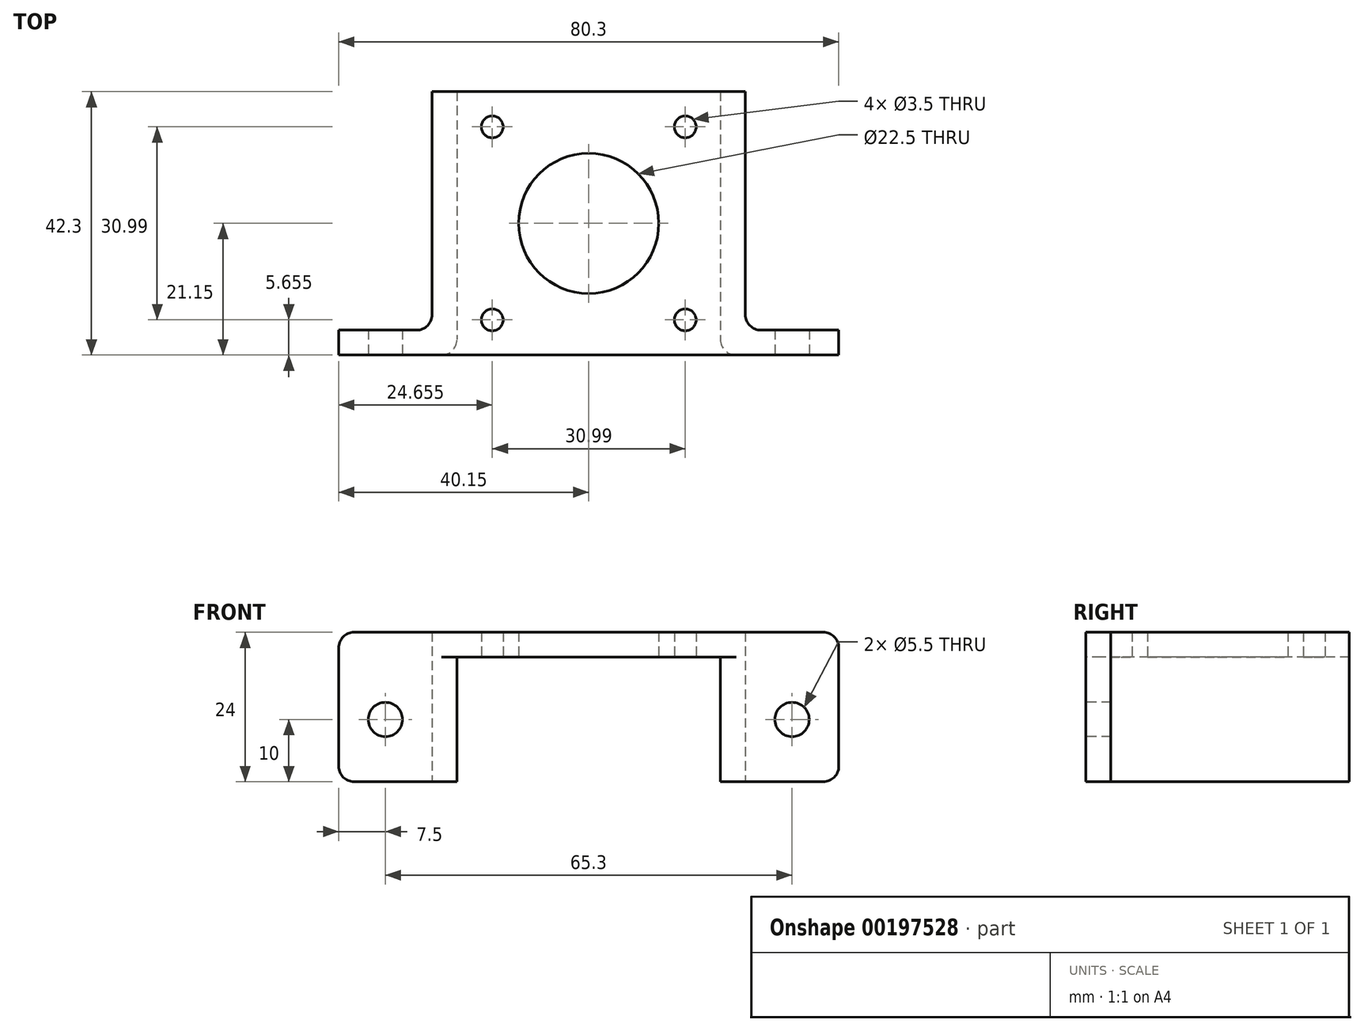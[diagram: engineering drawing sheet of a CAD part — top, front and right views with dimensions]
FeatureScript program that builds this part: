
annotation { "Feature Type Name" : "Feature", "Feature Type Description" : "" }
export const myFeature = defineFeature(function(context is Context, id is Id, definition is map)
    precondition{}
    {
        {
            var Q0;
            Q0=qCreatedBy(makeId("Top.planeOp"),FACE);
            var sketch = newSketch(context, id + "F0", { "sketchPlane" : qUnion([Q0])});
            skLineSegment(sketch, "E0.bottom", {"start": v(-21.15, 21.15) * mm, "end": v(21.15, 21.15) * mm});
            skLineSegment(sketch, "E0.left", {"start": v(-21.15, 21.15) * mm, "end": v(-21.15, -21.15) * mm, "construction": true});
            skLineSegment(sketch, "E0.right", {"start": v(21.15, 21.15) * mm, "end": v(21.15, -21.15) * mm, "construction": true});
            skLineSegment(sketch, "E1.bottom", {"start": v(-15.5, 15.5) * mm, "end": v(15.5, 15.5) * mm, "construction": true});
            skLineSegment(sketch, "E1.top", {"start": v(-15.5, -15.5) * mm, "end": v(15.5, -15.5) * mm, "construction": true});
            skLineSegment(sketch, "E1.left", {"start": v(-15.5, 15.5) * mm, "end": v(-15.5, -15.5) * mm, "construction": true});
            skLineSegment(sketch, "E1.right", {"start": v(15.5, 15.5) * mm, "end": v(15.5, -15.5) * mm, "construction": true});
            skCircle(sketch, "E2", {"center": v(-15.5, 15.5) * mm, "radius": 1.75 * mm});
            skCircle(sketch, "E3", {"center": v(-15.5, -15.5) * mm, "radius": 1.75 * mm});
            skCircle(sketch, "E4", {"center": v(15.5, 15.5) * mm, "radius": 1.75 * mm});
            skCircle(sketch, "E5", {"center": v(15.5, -15.5) * mm, "radius": 1.75 * mm});
            skCircle(sketch, "E6", {"center": v(0, 0) * mm, "radius": 11.25 * mm});
            skLineSegment(sketch, "E7", {"start": v(-21.15, -21.15) * mm, "end": v(21.15, -21.15) * mm});
            skLineSegment(sketch, "E8.bottom", {"start": v(21.15, -21.15) * mm, "end": v(40.15, -21.15) * mm});
            skLineSegment(sketch, "E8.top", {"start": v(21.15, -17.15) * mm, "end": v(40.15, -17.15) * mm});
            skLineSegment(sketch, "E8.left", {"start": v(21.15, -21.15) * mm, "end": v(21.15, -17.15) * mm});
            skLineSegment(sketch, "E8.right", {"start": v(40.15, -21.15) * mm, "end": v(40.15, -17.15) * mm});
            skLineSegment(sketch, "E9.bottom", {"start": v(-21.15, -21.15) * mm, "end": v(-40.15, -21.15) * mm});
            skLineSegment(sketch, "E9.top", {"start": v(-21.15, -17.15) * mm, "end": v(-40.15, -17.15) * mm});
            skLineSegment(sketch, "E9.left", {"start": v(-21.15, -21.15) * mm, "end": v(-21.15, -17.15) * mm});
            skLineSegment(sketch, "E9.right", {"start": v(-40.15, -21.15) * mm, "end": v(-40.15, -17.15) * mm});
            skLineSegment(sketch, "E10.bottom", {"start": v(-21.15, 21.15) * mm, "end": v(-25.15, 21.15) * mm});
            skLineSegment(sketch, "E10.top", {"start": v(-21.15, -17.15) * mm, "end": v(-25.15, -17.15) * mm});
            skLineSegment(sketch, "E10.left", {"start": v(-21.15, 21.15) * mm, "end": v(-21.15, -17.15) * mm});
            skLineSegment(sketch, "E10.right", {"start": v(-25.15, 21.15) * mm, "end": v(-25.15, -17.15) * mm});
            skLineSegment(sketch, "E11.bottom", {"start": v(21.15, 21.15) * mm, "end": v(25.15, 21.15) * mm});
            skLineSegment(sketch, "E11.top", {"start": v(21.15, -17.15) * mm, "end": v(25.15, -17.15) * mm});
            skLineSegment(sketch, "E11.left", {"start": v(21.15, 21.15) * mm, "end": v(21.15, -17.15) * mm});
            skLineSegment(sketch, "E11.right", {"start": v(25.15, 21.15) * mm, "end": v(25.15, -17.15) * mm});
            skSolve(sketch);
        }
        {
            var Q0;
            Q0=qSketchRegion(id+"F0",true);
            extrude(context, id + "F1", {"entities" : qUnion([Q0]), "depth" : 4 * mm});
        }
        {
            var Q0;
            Q0=makeQuery(id+"F1.opExtrude","CAP_FACE",FACE,{"disambiguationData":[OSD([sQuery(id+"F0.wireOp",EDGE,"E0.bottom"),sQuery(id+"F0.wireOp",EDGE,"E2"),sQuery(id+"F0.wireOp",EDGE,"E3"),sQuery(id+"F0.wireOp",EDGE,"E4"),sQuery(id+"F0.wireOp",EDGE,"E5"),sQuery(id+"F0.wireOp",EDGE,"E6"),sQuery(id+"F0.wireOp",EDGE,"E7"),sQuery(id+"F0.wireOp",EDGE,"E8.bottom"),sQuery(id+"F0.wireOp",EDGE,"E8.top"),sQuery(id+"F0.wireOp",EDGE,"E8.right"),sQuery(id+"F0.wireOp",EDGE,"E9.bottom"),sQuery(id+"F0.wireOp",EDGE,"E9.top"),sQuery(id+"F0.wireOp",EDGE,"E9.right"),sQuery(id+"F0.wireOp",EDGE,"E10.bottom"),sQuery(id+"F0.wireOp",EDGE,"E10.right"),sQuery(id+"F0.wireOp",EDGE,"E11.bottom"),sQuery(id+"F0.wireOp",EDGE,"E11.right")])],"isStart":true});
            var sketch = newSketch(context, id + "F2", { "sketchPlane" : qUnion([Q0])});
            skLineSegment(sketch, "E12.0", {"start": v(-21.15, -21.15) * mm, "end": v(-21.15, 17.15) * mm});
            skLineSegment(sketch, "E13.0", {"start": v(-21.15, 21.15) * mm, "end": v(-21.15, 17.15) * mm});
            skLineSegment(sketch, "E14.0", {"start": v(-21.15, 21.15) * mm, "end": v(-40.15, 21.15) * mm});
            skLineSegment(sketch, "E15.0", {"start": v(-40.15, 21.15) * mm, "end": v(-40.15, 17.15) * mm});
            skLineSegment(sketch, "E16.0", {"start": v(-25.15, -21.15) * mm, "end": v(-25.15, 17.15) * mm});
            skLineSegment(sketch, "E17.0", {"start": v(-25.15, 17.15) * mm, "end": v(-40.15, 17.15) * mm});
            skLineSegment(sketch, "E18.0", {"start": v(-21.15, -21.15) * mm, "end": v(-25.15, -21.15) * mm});
            skLineSegment(sketch, "E19.0", {"start": v(21.15, -21.15) * mm, "end": v(25.15, -21.15) * mm});
            skLineSegment(sketch, "E20.0", {"start": v(21.15, -21.15) * mm, "end": v(21.15, 17.15) * mm});
            skLineSegment(sketch, "E21.0", {"start": v(25.15, -21.15) * mm, "end": v(25.15, 17.15) * mm});
            skLineSegment(sketch, "E22.0", {"start": v(25.15, 17.15) * mm, "end": v(40.15, 17.15) * mm});
            skLineSegment(sketch, "E23.0", {"start": v(40.15, 21.15) * mm, "end": v(40.15, 17.15) * mm});
            skLineSegment(sketch, "E24.0", {"start": v(21.15, 21.15) * mm, "end": v(40.15, 21.15) * mm});
            skLineSegment(sketch, "E25.0", {"start": v(21.15, 21.15) * mm, "end": v(21.15, 17.15) * mm});
            skPoint(sketch, "E26.orphan", {"position": v(-21.15, 17.15) * mm});
            skPoint(sketch, "E27.orphan", {"position": v(21.15, 17.15) * mm});
            skSolve(sketch);
        }
        {
            var Q0;
            Q0=qSketchRegion(id+"F2",true);
            extrude(context, id + "F3", {"entities" : qUnion([Q0]), "operationType" : NewBodyOperationType.ADD, "depth" : 20 * mm});
        }
        {
            var Q0;
            Q0=makeQuery(id+"F3.boolean.opBoolean","MERGE",FACE,{"derivedFrom":[makeQuery(id+"F1.opExtrude","SWEPT_FACE",FACE,{"disambiguationData":[OSD([sQuery(id+"F0.wireOp",EDGE,"E7"),sQuery(id+"F0.wireOp",EDGE,"E8.bottom"),sQuery(id+"F0.wireOp",EDGE,"E9.bottom")])]}),makeQuery(id+"F3.opExtrude","SWEPT_FACE",FACE,{"disambiguationData":[OSD([sQuery(id+"F2.wireOp",EDGE,"E14.0")])]}),makeQuery(id+"F3.opExtrude","SWEPT_FACE",FACE,{"disambiguationData":[OSD([sQuery(id+"F2.wireOp",EDGE,"E24.0")])]})]});
            var sketch = newSketch(context, id + "F4", { "sketchPlane" : qUnion([Q0])});
            skCircle(sketch, "E28", {"center": v(-32.65, -10) * mm, "radius": 2.75 * mm});
            skPoint(sketch, "E28.centerSnap1", {"position": v(-21.15, -10) * mm});
            skCircle(sketch, "E29", {"center": v(32.65, -10) * mm, "radius": 2.75 * mm});
            skPoint(sketch, "E29.centerSnap0", {"position": v(21.15, -10) * mm});
            skSolve(sketch);
        }
        {
            var Q0;
            Q0=qSketchRegion(id+"F4",true);
            extrude(context, id + "F5", {"entities" : qUnion([Q0]), "operationType" : NewBodyOperationType.REMOVE, "endBound" : BoundingType.UP_TO_NEXT, "oppositeDirection" : true, "depth" : 25 * mm});
        }
        {
            var Q0;
            Q0=makeQuery(id+"F1.opExtrude","CAP_EDGE",EDGE,{"disambiguationData":[OSD([sQuery(id+"F0.wireOp",EDGE,"E9.right")])],"isStart":false});
            var Q1;
            Q1=makeQuery(id+"F3.opExtrude","CAP_EDGE",EDGE,{"disambiguationData":[OSD([sQuery(id+"F2.wireOp",EDGE,"E15.0")])],"isStart":false});
            var Q2;
            Q2=makeQuery(id+"F3.opExtrude","CAP_EDGE",EDGE,{"disambiguationData":[OSD([sQuery(id+"F2.wireOp",EDGE,"E23.0")])],"isStart":false});
            var Q3;
            Q3=makeQuery(id+"F1.opExtrude","CAP_EDGE",EDGE,{"disambiguationData":[OSD([sQuery(id+"F0.wireOp",EDGE,"E8.right")])],"isStart":false});
            var Q4;
            Q4=makeQuery(id+"F3.boolean.opBoolean","MERGE",EDGE,{"derivedFrom":[makeQuery(id+"F1.opExtrude","SWEPT_EDGE",EDGE,{"disambiguationData":[OSD([sQuery(id+"F0.wireOp",EDGE,"E8.top"),sQuery(id+"F0.wireOp",EDGE,"E11.top"),sQuery(id+"F0.wireOp",EDGE,"E11.right")])]}),makeQuery(id+"F3.opExtrude","SWEPT_EDGE",EDGE,{"disambiguationData":[OSD([sQuery(id+"F2.wireOp",EDGE,"E21.0"),sQuery(id+"F2.wireOp",EDGE,"E22.0")])]})]});
            var Q5;
            Q5=makeQuery(id+"F3.boolean.opBoolean","MERGE",EDGE,{"derivedFrom":[makeQuery(id+"F1.opExtrude","SWEPT_EDGE",EDGE,{"disambiguationData":[OSD([sQuery(id+"F0.wireOp",EDGE,"E9.top"),sQuery(id+"F0.wireOp",EDGE,"E10.top"),sQuery(id+"F0.wireOp",EDGE,"E10.right")])]}),makeQuery(id+"F3.opExtrude","SWEPT_EDGE",EDGE,{"disambiguationData":[OSD([sQuery(id+"F2.wireOp",EDGE,"E16.0"),sQuery(id+"F2.wireOp",EDGE,"E17.0")])]})]});
            var Q6;
            Q6=makeQuery(id+"F3.opExtrude","SWEPT_EDGE",EDGE,{"disambiguationData":[OSD([sQuery(id+"F0.wireOp",EDGE,"E7"),sQuery(id+"F0.wireOp",EDGE,"E8.bottom"),sQuery(id+"F0.wireOp",EDGE,"E9.bottom"),sQuery(id+"F2.wireOp",EDGE,"E24.0"),sQuery(id+"F2.wireOp",EDGE,"E25.0")])]});
            var Q7;
            Q7=makeQuery(id+"F3.opExtrude","SWEPT_EDGE",EDGE,{"disambiguationData":[OSD([sQuery(id+"F0.wireOp",EDGE,"E7"),sQuery(id+"F0.wireOp",EDGE,"E8.bottom"),sQuery(id+"F0.wireOp",EDGE,"E9.bottom"),sQuery(id+"F2.wireOp",EDGE,"E13.0"),sQuery(id+"F2.wireOp",EDGE,"E14.0")])]});
            fillet(context, id + "F6", {"entities" : qUnion([Q0, Q1, Q2, Q3, Q4, Q5, Q6, Q7]), "radius" : 2.5 * mm, "tangentPropagation" : true, "allowEdgeOverflow" : false});
        }
    });
